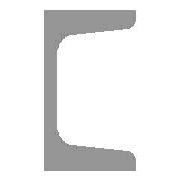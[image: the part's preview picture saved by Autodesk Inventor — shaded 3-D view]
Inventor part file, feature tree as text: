
AUTODESK INVENTOR PART (.ipt)
format: ipt  version: 2017 (Build 210142000, 142)  size: 140,288 bytes
history: native  units: mm (DEFAULTED — no unit token found)
features: other x4, plane x2, sketch x2, split x1
ambient origin geometry x8: Origin, YZ Plane, XZ Plane, XY Plane, X Axis, Y Axis, Z Axis, Center Point
bodies: Solid1 (feature_tree), Body (feature_tree)
feature tree (9):
  parser-record x1  (decoder bookkeeping rows leaked as tree rows — omitted from the tree; the rows remain in map.json)
  other  "Driven Length"
  other  "Start plane"
  other  "End plane"
  plane  "Work Plane4"
  split  "Split1"
  sketch  "Sketch3"  dims[d0=4.6736mm]
  plane  "Work Plane3"
  sketch  "Sketch4"  dims[d1=50.8mm d2=40.2336mm d3=7.5184mm d4=17.682845mm d5=0.926581mm d6=2438.4mm d7=0.0mm d25=0.0mm d26=-0.0mm d27=2438.4mm d28=6.712646mm d29=2.2352mm d30=90.0deg d31=2438.4mm]
